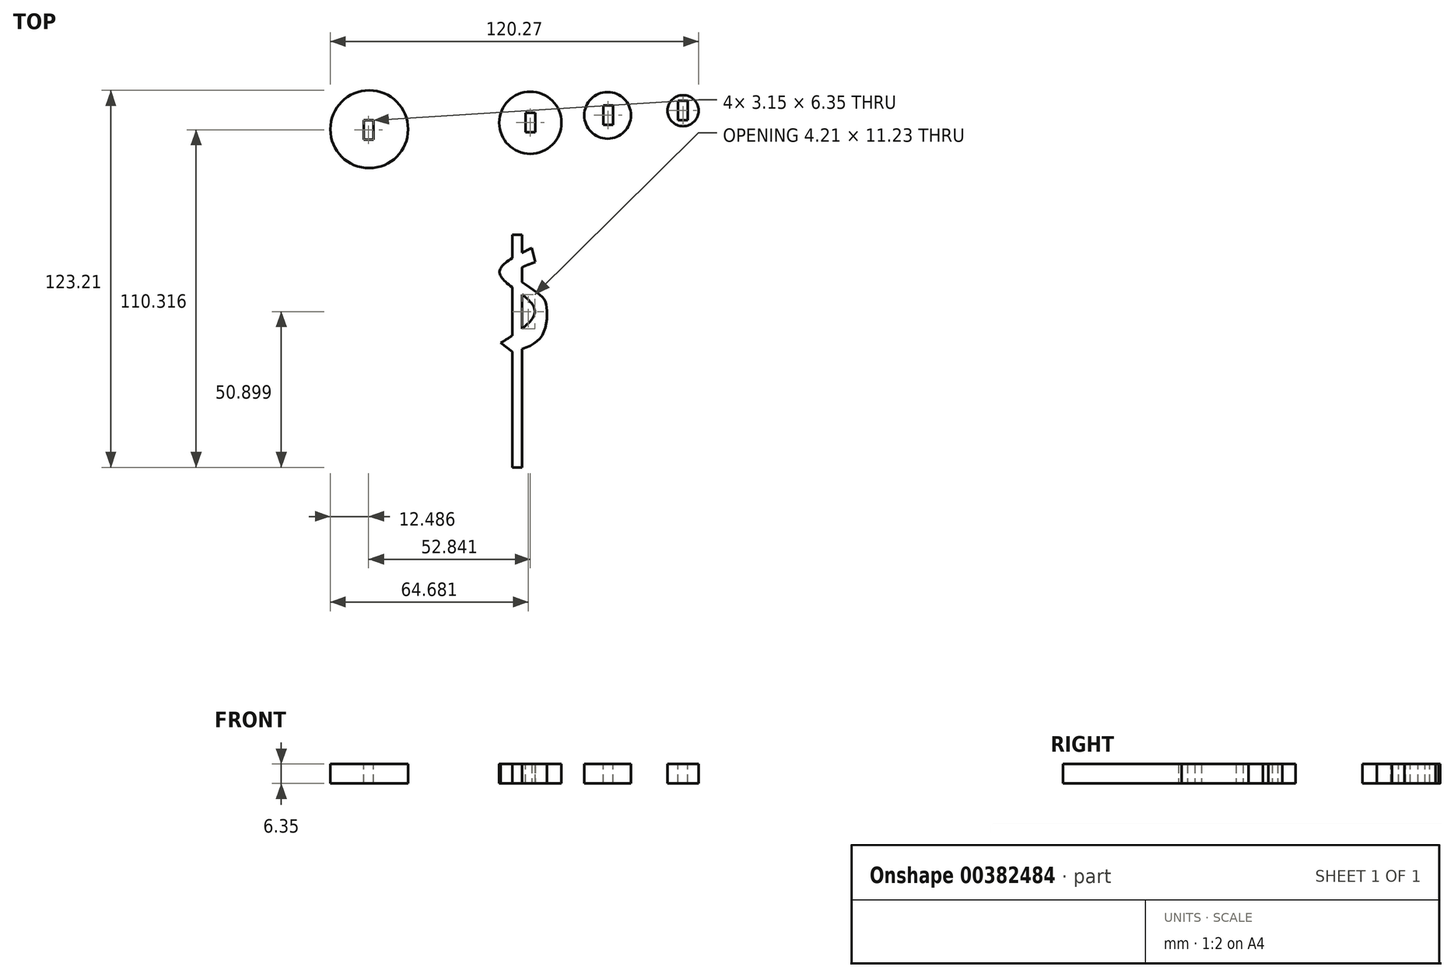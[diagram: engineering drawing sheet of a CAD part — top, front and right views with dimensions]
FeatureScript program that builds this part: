
annotation { "Feature Type Name" : "Feature", "Feature Type Description" : "" }
export const myFeature = defineFeature(function(context is Context, id is Id, definition is map)
    precondition{}
    {
        {
            var Q0;
            Q0=qCreatedBy(makeId("Top.planeOp"),FACE);
            var sketch = newSketch(context, id + "F0", { "sketchPlane" : qUnion([Q0])});
            skCircle(sketch, "E0", {"center": v(-62.65, 47.44) * mm, "radius": 12.7 * mm});
            skCircle(sketch, "E1", {"center": v(-10.04, 49.57) * mm, "radius": 10.16 * mm});
            skCircle(sketch, "E2", {"center": v(15.2, 52) * mm, "radius": 7.62 * mm});
            skCircle(sketch, "E3", {"center": v(39.84, 53.52) * mm, "radius": 5.08 * mm});
            skSolve(sketch);
        }
        {
            var Q0;
            Q0 = qSketchRegion(id + "F0", true);
            extrude(context, id + "F1", {"entities" : qUnion([Q0]), "depth" : 6.35 * mm});
        }
        {
            var Q0;
            Q0=qCreatedBy(makeId("Top.planeOp"),FACE);
            var sketch = newSketch(context, id + "F2", { "sketchPlane" : qUnion([Q0])});
            skFitSpline(sketch, "E4", {"points": [v(-9.62, 8.61) * mm, v(-19.95, 0) * mm, v(-8.75, -10.9) * mm, v(-19.66, -22.39) * mm], "startDerivative": vector(-53.69, -26.1) * mm, "endDerivative": vector(-53.69, -33.53) * mm});
            skFitSpline(sketch, "E5", {"points": [v(-8.47, 4.02) * mm, v(-14.78, 0) * mm, v(-7.32, -6.31) * mm, v(-4.74, -10.62) * mm, v(-6.46, -20.38) * mm, v(-15.93, -25.26) * mm], "startDerivative": vector(-51.93, -18.78) * mm, "endDerivative": vector(-50.14, -13.77) * mm});
            skLineSegment(sketch, "E6", {"start": v(-19.66, -22.39) * mm, "end": v(-15.93, -25.26) * mm});
            skLineSegment(sketch, "E7", {"start": v(-9.62, 8.61) * mm, "end": v(-8.47, 4.02) * mm});
            skLineSegment(sketch, "E8", {"start": v(-12.77, 12.92) * mm, "end": v(-12.77, -37.67) * mm});
            skLineSegment(sketch, "E9", {"start": v(-12.77, -37.67) * mm, "end": v(-12.77, -63.07) * mm});
            skLineSegment(sketch, "E10", {"start": v(-12.77, 12.92) * mm, "end": v(-15.92, 12.92) * mm});
            skLineSegment(sketch, "E11", {"start": v(-15.92, 12.92) * mm, "end": v(-15.92, -63.07) * mm});
            skLineSegment(sketch, "E12", {"start": v(-15.92, -63.07) * mm, "end": v(-12.77, -63.07) * mm});
            skSolve(sketch);
        }
        {
            var Q0;
            Q0 = qSketchRegion(id + "F2", true);
            extrude(context, id + "F3", {"entities" : qUnion([Q0]), "depth" : 6.35 * mm});
        }
        {
            var Q0;
            Q0=makeQuery(id+"F1.opExtrude","CAP_FACE",FACE,{"disambiguationData":[OSD([sQuery(id+"F0.wireOp",EDGE,"E3")])],"isStart":false});
            var sketch = newSketch(context, id + "F4", { "sketchPlane" : qUnion([Q0])});
            skLineSegment(sketch, "E13", {"start": v(41.35, 50.36) * mm, "end": v(38.2, 50.36) * mm});
            skLineSegment(sketch, "E14", {"start": v(41.35, 50.36) * mm, "end": v(41.35, 56.71) * mm});
            skLineSegment(sketch, "E15", {"start": v(38.2, 50.36) * mm, "end": v(38.2, 56.71) * mm});
            skLineSegment(sketch, "E16", {"start": v(41.35, 56.71) * mm, "end": v(38.2, 56.71) * mm});
            skCircle(sketch, "E17", {"center": v(39.84, 53.52) * mm, "radius": 7.42 * mm});
            skSolve(sketch);
        }
        {
            var Q0;
            Q0=makeQuery(id+"F1.opExtrude","CAP_FACE",FACE,{"disambiguationData":[OSD([sQuery(id+"F0.wireOp",EDGE,"E2")])],"isStart":false});
            var sketch = newSketch(context, id + "F5", { "sketchPlane" : qUnion([Q0])});
            skLineSegment(sketch, "E18", {"start": v(16.94, 48.9) * mm, "end": v(13.8, 48.9) * mm});
            skLineSegment(sketch, "E19", {"start": v(16.94, 48.9) * mm, "end": v(16.94, 55.24) * mm});
            skLineSegment(sketch, "E20", {"start": v(13.8, 48.9) * mm, "end": v(13.8, 55.24) * mm});
            skLineSegment(sketch, "E21", {"start": v(16.94, 55.24) * mm, "end": v(13.8, 55.24) * mm});
            skSolve(sketch);
        }
        {
            var Q0;
            Q0=makeQuery(id+"F1.opExtrude","CAP_FACE",FACE,{"disambiguationData":[OSD([sQuery(id+"F0.wireOp",EDGE,"E1")])],"isStart":false});
            var sketch = newSketch(context, id + "F6", { "sketchPlane" : qUnion([Q0])});
            skLineSegment(sketch, "E22", {"start": v(-8.45, 46.53) * mm, "end": v(-11.6, 46.53) * mm});
            skLineSegment(sketch, "E23", {"start": v(-8.45, 46.53) * mm, "end": v(-8.45, 52.88) * mm});
            skLineSegment(sketch, "E24", {"start": v(-11.6, 46.53) * mm, "end": v(-11.6, 52.88) * mm});
            skLineSegment(sketch, "E25", {"start": v(-8.45, 52.88) * mm, "end": v(-11.6, 52.88) * mm});
            skSolve(sketch);
        }
        {
            var Q0;
            Q0=makeQuery(id+"F1.opExtrude","CAP_FACE",FACE,{"disambiguationData":[OSD([sQuery(id+"F0.wireOp",EDGE,"E0")])],"isStart":false});
            var sketch = newSketch(context, id + "F7", { "sketchPlane" : qUnion([Q0])});
            skLineSegment(sketch, "E26", {"start": v(-61.29, 44.07) * mm, "end": v(-64.44, 44.07) * mm});
            skLineSegment(sketch, "E27", {"start": v(-61.29, 44.07) * mm, "end": v(-61.29, 50.42) * mm});
            skLineSegment(sketch, "E28", {"start": v(-64.44, 44.07) * mm, "end": v(-64.44, 50.42) * mm});
            skLineSegment(sketch, "E29", {"start": v(-61.29, 50.42) * mm, "end": v(-64.44, 50.42) * mm});
            skSolve(sketch);
        }
        {
            var Q0;
            Q0=makeQuery(id+"F6.imprint","IMPRINT",FACE,{"disambiguationData":[TD([[makeQuery(id+"F6.imprint","IMPRINT",EDGE,{"derivedFrom":sQuery(id+"F6.wireOp",EDGE,"E22")}),-1.0]])]});
            var Q1;
            Q1=makeQuery(id+"F5.imprint","IMPRINT",FACE,{"disambiguationData":[TD([[makeQuery(id+"F5.imprint","IMPRINT",EDGE,{"derivedFrom":sQuery(id+"F5.wireOp",EDGE,"E18")}),-1.0]])]});
            var Q2;
            Q2=makeQuery(id+"F4.imprint","IMPRINT",FACE,{"disambiguationData":[TD([[makeQuery(id+"F4.imprint","IMPRINT",EDGE,{"derivedFrom":sQuery(id+"F4.wireOp",EDGE,"E13")}),-1.0]])]});
            extrude(context, id + "F8", {"entities" : qUnion([Q0, Q1, Q2]), "operationType" : NewBodyOperationType.REMOVE, "oppositeDirection" : true, "depth" : 25.4 * mm});
        }
        {
            var Q0;
            Q0=makeQuery(id+"F7.imprint","IMPRINT",FACE,{"disambiguationData":[TD([[makeQuery(id+"F7.imprint","IMPRINT",EDGE,{"derivedFrom":sQuery(id+"F7.wireOp",EDGE,"E26")}),-1.0]])]});
            extrude(context, id + "F9", {"entities" : qUnion([Q0]), "operationType" : NewBodyOperationType.REMOVE, "oppositeDirection" : true, "depth" : 6.35 * mm});
        }
    });
